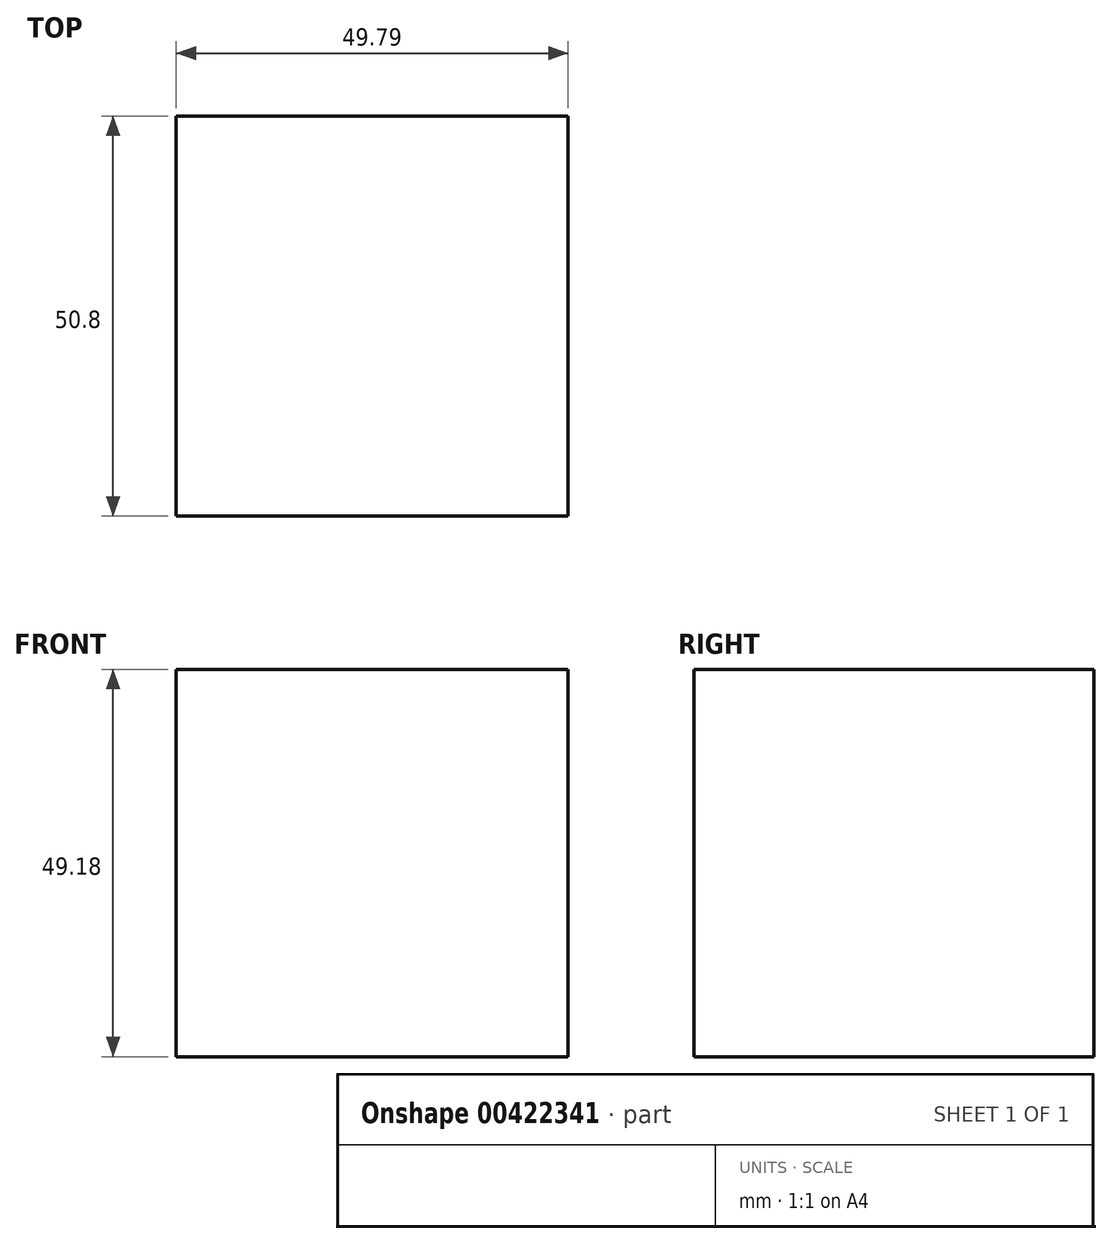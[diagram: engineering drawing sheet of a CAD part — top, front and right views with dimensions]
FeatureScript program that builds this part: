
annotation { "Feature Type Name" : "Feature", "Feature Type Description" : "" }
export const myFeature = defineFeature(function(context is Context, id is Id, definition is map)
    precondition{}
    {
        {
            var Q0;
            Q0=qCreatedBy(makeId("Front.planeOp"),FACE);
            var sketch = newSketch(context, id + "F0", { "sketchPlane" : qUnion([Q0])});
            skLineSegment(sketch, "E0.bottom", {"start": v(0, 0) * mm, "end": v(-49.8, 0) * mm});
            skLineSegment(sketch, "E0.top", {"start": v(0, 49.18) * mm, "end": v(-49.8, 49.18) * mm});
            skLineSegment(sketch, "E0.left", {"start": v(0, 0) * mm, "end": v(0, 49.18) * mm});
            skLineSegment(sketch, "E0.right", {"start": v(-49.8, 0) * mm, "end": v(-49.8, 49.18) * mm});
            skSolve(sketch);
        }
        {
            var Q0;
            Q0 = qSketchRegion(id + "F0", true);
            extrude(context, id + "F1", {"entities" : qUnion([Q0]), "depth" : 50.8 * mm});
        }
    });
